# Revit family: Cim731
name_source: partatom
category: Pipe Accessories
revit_build: Autodesk Revit 2016 (Build: 20150220_1215(x64)
units: mm (PartAtom-declared; Revit-internal decimal feet)

## family parameters
Always vertical = Yes
Cut with Voids When Loaded = No
OmniClass Number = 23.75.00.00
OmniClass Title = Climate Control (HVAC)
Part Type = Normal
Round Connector Dimension = Use Diameter
Shared = No
Work Plane-Based = No

## types (5) — shared parameters
A = 80 mm  [stored 0.262467 ft]
Ottone = Ottone
Plastica bianca = Plastica bianca
Plastica blu = Plastica blu
Plastica nera = Plastica nera
Plastica rossa = Plastica rossa
Pressione nominale = 25
Temperatura di esercizio = -10 ÷ 120 °C

## per-type parameters (varying)
| type | 2d | B | B1 | C | CH | CH/2-1 | D | D2 | DN | E | d | dn | dss | f1 | f2 | r | rr |
| 1/2''x1/2" | 15 mm  [stored 0.0492126 ft] | 77 mm  [stored 0.252625 ft] | 29 mm  [stored 0.0951444 ft] | 42 mm  [stored 0.137795 ft] | 16 mm | 15 mm  [stored 0.0492126 ft] | 14 mm  [stored 0.0459318 ft] | 8 mm  [stored 0.0262467 ft] | 10 mm  [stored 0.0328084 ft] | 100 mm | 8 mm  [stored 0.0262467 ft] | 9 mm  [stored 0.0295276 ft] | 29 mm  [stored 0.0951444 ft] | 60 mm | 17 mm  [stored 0.0557743 ft] | 12 mm  [stored 0.0393701 ft] | 11 mm  [stored 0.0360892 ft] |
| 3/4"x3/4" | 20 mm  [stored 0.0656168 ft] | 81 mm  [stored 0.265748 ft] | 33 mm  [stored 0.108268 ft] | 61 mm | 19 mm  [stored 0.062336 ft] | 18 mm | 15 mm  [stored 0.0492126 ft] | 11 mm  [stored 0.0360892 ft] | 12 mm  [stored 0.0393701 ft] | 100 mm | 10 mm  [stored 0.0328084 ft] | 11 mm  [stored 0.0360892 ft] | 38 mm | 64 mm | 19 mm  [stored 0.062336 ft] | 15 mm  [stored 0.0492126 ft] | 14 mm  [stored 0.0459318 ft] |
| 1"x1" | 25 mm  [stored 0.082021 ft] | 85 mm  [stored 0.278871 ft] | 35 mm  [stored 0.114829 ft] | 78 mm  [stored 0.255906 ft] | 24 mm  [stored 0.0787402 ft] | 23 mm  [stored 0.0754593 ft] | 21 mm  [stored 0.0688976 ft] | 12 mm  [stored 0.0393701 ft] | 16 mm | 150 mm | 13 mm | 15 mm  [stored 0.0492126 ft] | 47 mm  [stored 0.154199 ft] | 68 mm  [stored 0.223097 ft] | 23 mm  [stored 0.0754593 ft] | 19 mm  [stored 0.062336 ft] | 18 mm |
| 1"1/4x1"1/4 | 25 mm  [stored 0.082021 ft] | 85 mm  [stored 0.278871 ft] | 38 mm | 88 mm  [stored 0.288714 ft] | 26 mm | 25 mm  [stored 0.082021 ft] | 24 mm  [stored 0.0787402 ft] | 13 mm | 19 mm  [stored 0.062336 ft] | 175 mm | 13 mm | 18 mm | 52 mm  [stored 0.170604 ft] | 68 mm  [stored 0.223097 ft] | 26 mm | 22 mm  [stored 0.0721785 ft] | 21 mm  [stored 0.0688976 ft] |
| 1"1/2x1"1/2 | 25 mm  [stored 0.082021 ft] | 85 mm  [stored 0.278871 ft] | 38 mm | 94 mm | 32 mm  [stored 0.104987 ft] | 31 mm  [stored 0.101706 ft] | 26 mm | 14 mm  [stored 0.0459318 ft] | 21 mm  [stored 0.0688976 ft] | 175 mm | 13 mm | 20 mm  [stored 0.0656168 ft] | 55 mm | 68 mm  [stored 0.223097 ft] | 29 mm  [stored 0.0951444 ft] | 25 mm  [stored 0.082021 ft] | 24 mm  [stored 0.0787402 ft] |

note: [stored X ft] marks values corroborated as IEEE doubles in the binary element streams (Revit-internal decimal feet)

## geometry (parser evidence)
native form markers: Sweep x7
no freeform markers — native parametric forms only
